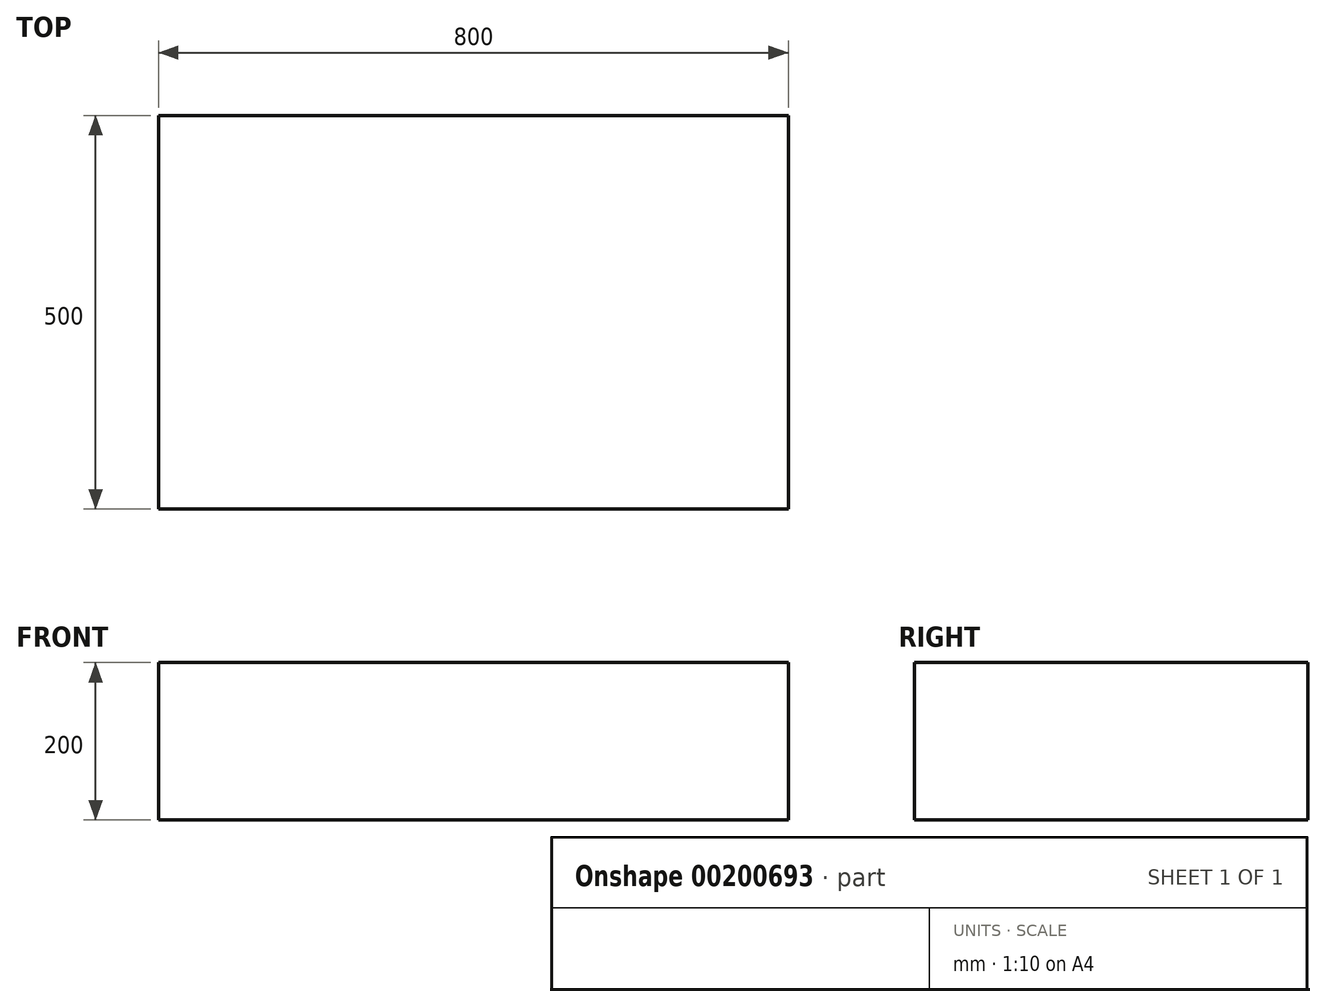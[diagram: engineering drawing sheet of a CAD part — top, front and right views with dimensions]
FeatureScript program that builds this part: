
annotation { "Feature Type Name" : "Feature", "Feature Type Description" : "" }
export const myFeature = defineFeature(function(context is Context, id is Id, definition is map)
    precondition{}
    {
        {
            var Q0;
            Q0=qCreatedBy(makeId("Front.planeOp"),FACE);
            var sketch = newSketch(context, id + "F0", { "sketchPlane" : qUnion([Q0])});
            skLineSegment(sketch, "E0.bottom", {"start": v(0, 0) * mm, "end": v(800, 0) * mm});
            skLineSegment(sketch, "E0.top", {"start": v(0, 200) * mm, "end": v(800, 200) * mm});
            skLineSegment(sketch, "E0.left", {"start": v(0, 0) * mm, "end": v(0, 200) * mm});
            skLineSegment(sketch, "E0.right", {"start": v(800, 0) * mm, "end": v(800, 200) * mm});
            skSolve(sketch);
        }
        {
            var Q0;
            Q0=qSketchRegion(id+"F0",true);
            extrude(context, id + "F1", {"entities" : qUnion([Q0]), "depth" : 500 * mm});
        }
    });
